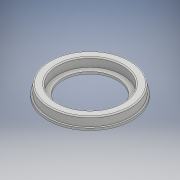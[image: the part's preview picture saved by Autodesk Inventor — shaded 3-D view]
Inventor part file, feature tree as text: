
AUTODESK INVENTOR PART (.ipt)
format: ipt  version: 2017 (Build 210142000, 142)  size: 136,704 bytes
history: native  units: mm
features: extrude x2, sketch x1, fillet x1
ambient origin geometry x8: Origin, YZ Plane, XZ Plane, XY Plane, X Axis, Y Axis, Z Axis, Center Point
bodies: Solid1 (feature_tree)
feature tree (4):
  sketch  "Sketch1"  dims[d0=29.7mm d1=37.0mm d2=38.5mm d3=5.0mm d4=0.0mm d5=1.0mm d6=0.0mm d7=0.5mm d8=25.0mm]
  extrude  "Extrusion1"  Depth=0.5mm
  extrude  "Extrusion2"  Depth=0.5mm
  fillet  "Fillet1"  Radius=5.0mm
